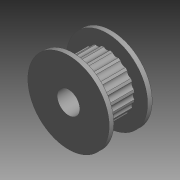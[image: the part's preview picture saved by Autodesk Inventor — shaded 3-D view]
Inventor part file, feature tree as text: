
AUTODESK INVENTOR PART (.ipt)
format: ipt  version: 2015 SP1 (Build 190203100, 203)  size: 155,648 bytes
history: native  units: mm
features: sketch x2, revolve x1, extrude x1, pattern_circular x1
ambient origin geometry x8: Origin, YZ Plane, XZ Plane, XY Plane, X Axis, Y Axis, Z Axis, Center Point
bodies: Solid1 (feature_tree)
feature tree (5):
  revolve  "Revolution1"  [1 undecoded]
  extrude  "Extrusion1"  Depth=9.0mm
  pattern_circular  "Circular Pattern1"  [2 undecoded]
  sketch  "Sketch1"  dims[d0=2.5mm d1=7.5mm]
  sketch  "Sketch2"  dims[d2=1.0mm d3=9.0mm d4=1.0mm d6=6.1mm d7=90.0deg d8=6.8mm d9=2.0mm d10=10.0mm d11=0.0mm d12=200.0mm d13=360.0deg]
note: 3 required parameter values undecoded (feature->parameter linkage not recoverable at this tier; creation-order binding heuristic only, values carry confidence <= 0.55)